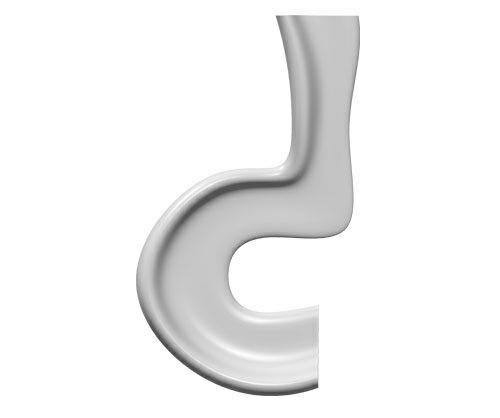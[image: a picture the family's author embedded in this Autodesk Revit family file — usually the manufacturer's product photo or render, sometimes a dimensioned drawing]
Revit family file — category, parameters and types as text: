
# Revit family: CITY ALPHABET letter „D”
name_source: partatom
category: Furniture
revit_build: Autodesk Revit 2018 (Build: 20190510_1515(x64)
units: mm (PartAtom-declared; Revit-internal decimal feet)

## family parameters
Cut with Voids When Loaded = No
Host = Face
OmniClass Number = 23.40.10.11.14
OmniClass Title = Exterior Seating
Room Calculation Point = No
Shared = No

## types (1)
- CITY ALPHABET letter „D”
    Default Elevation = 1219 mm
    Height = 750 mm  [stored 2.46063 ft]
    IfcExportAs = IfcFurnishingElement
    Length = 2500 mm  [stored 8.2021 ft]
    Manufacturer = Astrini Design
    Material information = Colour choice from RAL colour standard. Customer may inquire about specific request regarding individual order.
    Model = CITY ALPHABET letter „D”
    Operating temperature = -40°C to 80°C, ( -40°F to 176°F )
    Type Comments = Bench
    Type Image = D.jpg
    URL = https://astrini-design.pl
    Weight (approximately) = 73.00 kg
    Weight - filled (approximately) = 123.00 kg
    Width = 1470 mm

note: [stored X ft] marks values corroborated as IEEE doubles in the binary element streams (Revit-internal decimal feet)
